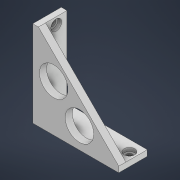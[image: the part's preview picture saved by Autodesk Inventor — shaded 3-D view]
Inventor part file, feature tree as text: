
AUTODESK INVENTOR PART (.ipt)
format: ipt  version: 2022 (Build 260153000, 153)  size: 141,824 bytes
history: native  units: mm
features: sketch x5, hole x3, extrude x2
ambient origin geometry x8: Origin, YZ Plane, XZ Plane, XY Plane, X Axis, Y Axis, Z Axis, Center Point
bodies: Volumenkörper1 (feature_tree)
feature tree (10):
  extrude  "Extrusion1"  Depth=45.0mm
  extrude  "Extrusion3"  Depth=8.0mm
  hole  "Bohrung1"  [1 undecoded]
  hole  "Bohrung2"  [1 undecoded]
  hole  "Bohrung3"  [1 undecoded]
  sketch  "Skizze1"  dims[d0=45.0mm d1=45.0mm]
  sketch  "Skizze2"  dims[d2=4.0mm d3=0.0mm]
  sketch  "Skizze4"  dims[d4=16.0mm d5=6.0mm d6=4.0mm d7=2.0mm d8=90.0deg d9=8.0mm d10=20.594885mm d11=9.5mm]
  sketch  "Skizze5"  dims[d12=9.5mm d14=22.0mm]
  sketch  "Skizze6"  dims[d15=22.0mm d20=3.2mm d21=3.2mm d22=16.0mm d23=0.0mm d24=3.5mm d25=6.0mm d26=6.0mm d27=2.0mm d28=90.0deg d29=8.0mm d30=20.594885mm d31=4.0mm d32=6.0mm d33=3.5mm d34=6.0mm d35=6.0mm d36=2.0mm d37=90.0deg d38=8.0mm d39=20.594885mm d40=6.0mm d41=4.0mm]
note: 3 required parameter values undecoded (feature->parameter linkage not recoverable at this tier; creation-order binding heuristic only, values carry confidence <= 0.55)
